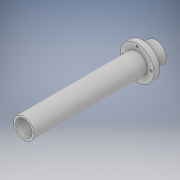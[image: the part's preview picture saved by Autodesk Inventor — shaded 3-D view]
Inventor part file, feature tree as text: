
AUTODESK INVENTOR PART (.ipt)
format: ipt  version: 2017 (Build 210142000, 142)  size: 125,440 bytes
history: native  units: in
note: dims shown in document units (in); Inventor stores cm internally (conversion verified against a paired STEP export)
features: sketch x5, extrude x3, hole x1, projected_geometry x1
ambient origin geometry x8: Origin, YZ Plane, XZ Plane, XY Plane, X Axis, Y Axis, Z Axis, Center Point
bodies: Body1 (feature_tree)
feature tree (10):
  sketch  "Sketch1"  dims[d0=0.495in d1=0.609in]
  extrude  "Extrusion2"  Depth=0.609in
  extrude  "Extrusion3"  Depth=3.937in TaperAngle=0.0deg
  extrude  "Extrusion4"  Depth=3.37in TaperAngle=0.0deg
  hole  "Hole1"  [1 undecoded]
  sketch  "Sketch5"  dims[d11=0.835in]
  sketch  "Sketch6"  dims[d12=0.062in d13=0.157in d14=0.375in d15=0.25in d16=0.5635in d17=0.248in d18=0.8108in]
  sketch  "Sketch3"  dims[d4=1.0in d5=3.937in d6=0.0in]
  projected_geometry  "Projected Loop1"
  sketch  "Sketch4"  dims[d7=0.394in d8=0.0in d9=3.37in d10=0.0in]
note: 1 required parameter value undecoded (feature->parameter linkage not recoverable at this tier; creation-order binding heuristic only, values carry confidence <= 0.55)
